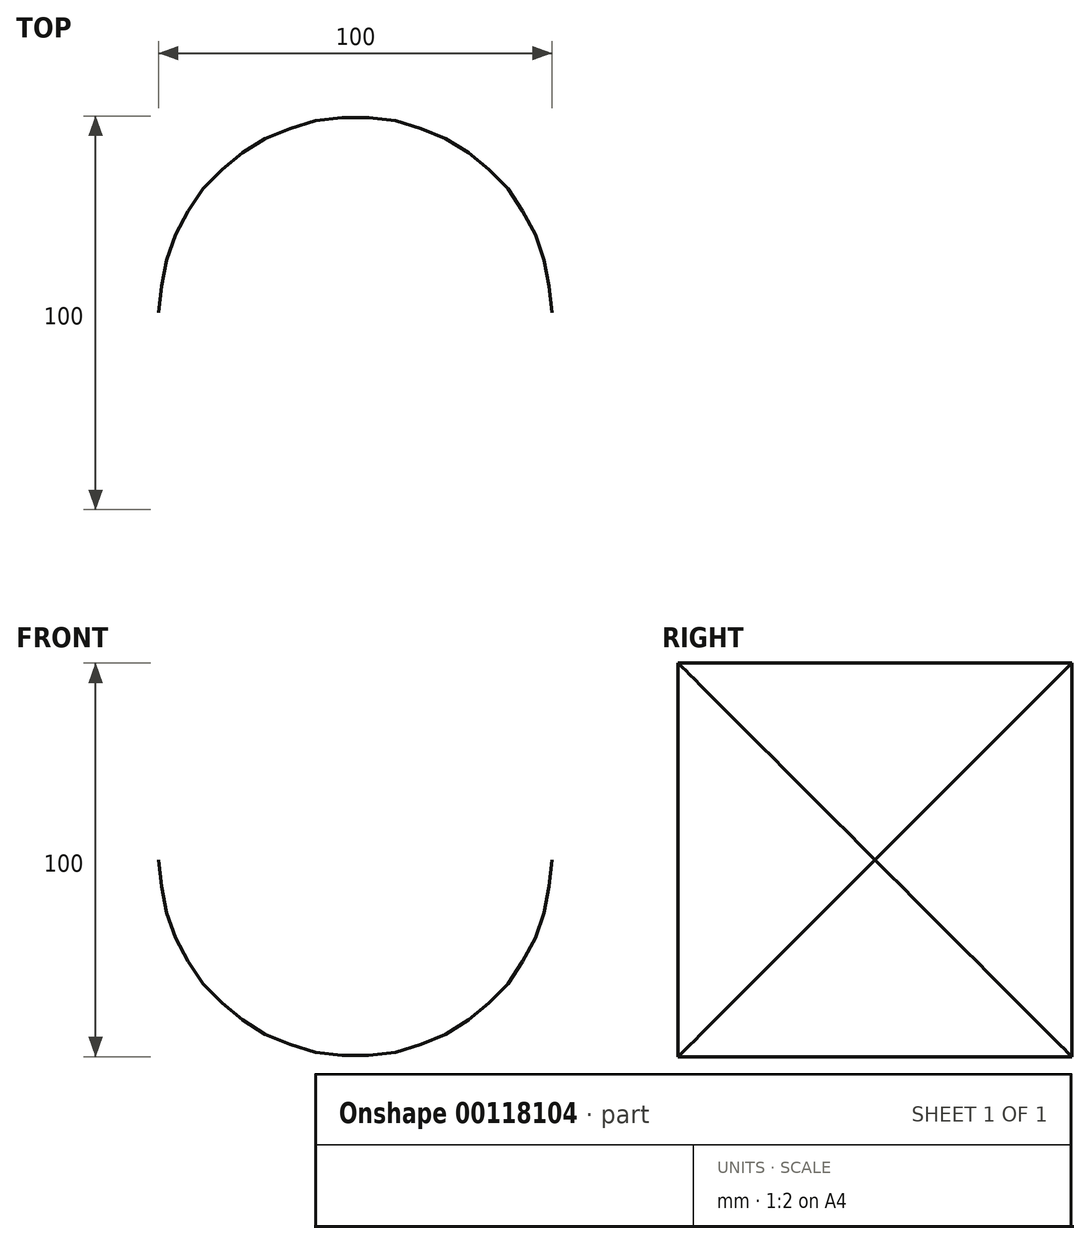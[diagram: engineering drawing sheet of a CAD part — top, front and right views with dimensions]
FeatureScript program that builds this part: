
annotation { "Feature Type Name" : "Feature", "Feature Type Description" : "" }
export const myFeature = defineFeature(function(context is Context, id is Id, definition is map)
    precondition{}
    {
        {
            var Q0;
            Q0=qCreatedBy(makeId("Top.planeOp"),FACE);
            var sketch = newSketch(context, id + "F0", { "sketchPlane" : qUnion([Q0])});
            skCircle(sketch, "E0", {"center": v(0, 0) * mm, "radius": 50 * mm});
            skSolve(sketch);
        }
        {
            var Q0;
            Q0=makeQuery(id+"F0.imprint","IMPRINT",FACE,{"disambiguationData":[TD([[makeQuery(id+"F0.imprint","IMPRINT",EDGE,{"derivedFrom":sQuery(id+"F0.wireOp",EDGE,"E0")}),1.0]])]});
            var Q1;
            Q1=sQuery(id+"F0.wireOp",EDGE,"E0");
            extrude(context, id + "F1", {"entities" : qUnion([Q0]), "surfaceEntities" : qUnion([Q1]), "depth" : 100 * mm});
        }
        {
            var Q0;
            Q0=qCreatedBy(makeId("Front.planeOp"),FACE);
            var sketch = newSketch(context, id + "F2", { "sketchPlane" : qUnion([Q0])});
            skCircle(sketch, "E1", {"center": v(0, 50) * mm, "radius": 50 * mm});
            skLineSegment(sketch, "E2.bottom", {"start": v(-83.24, 123.31) * mm, "end": v(96.35, 123.31) * mm});
            skLineSegment(sketch, "E2.top", {"start": v(-83.24, -28.4) * mm, "end": v(96.35, -28.4) * mm});
            skLineSegment(sketch, "E2.left", {"start": v(-83.24, 123.31) * mm, "end": v(-83.24, -28.4) * mm});
            skLineSegment(sketch, "E2.right", {"start": v(96.35, 123.31) * mm, "end": v(96.35, -28.4) * mm});
            skSolve(sketch);
        }
        {
            var Q0;
            Q0=makeQuery(id+"F2.imprint","IMPRINT",FACE,{"disambiguationData":[TD([[makeQuery(id+"F2.imprint","IMPRINT",EDGE,{"derivedFrom":sQuery(id+"F2.wireOp",EDGE,"E1")}),-1.0]])]});
            extrude(context, id + "F3", {"entities" : qUnion([Q0]), "operationType" : NewBodyOperationType.REMOVE, "endBound" : BoundingType.SYMMETRIC, "depth" : 100 * mm});
        }
    });
